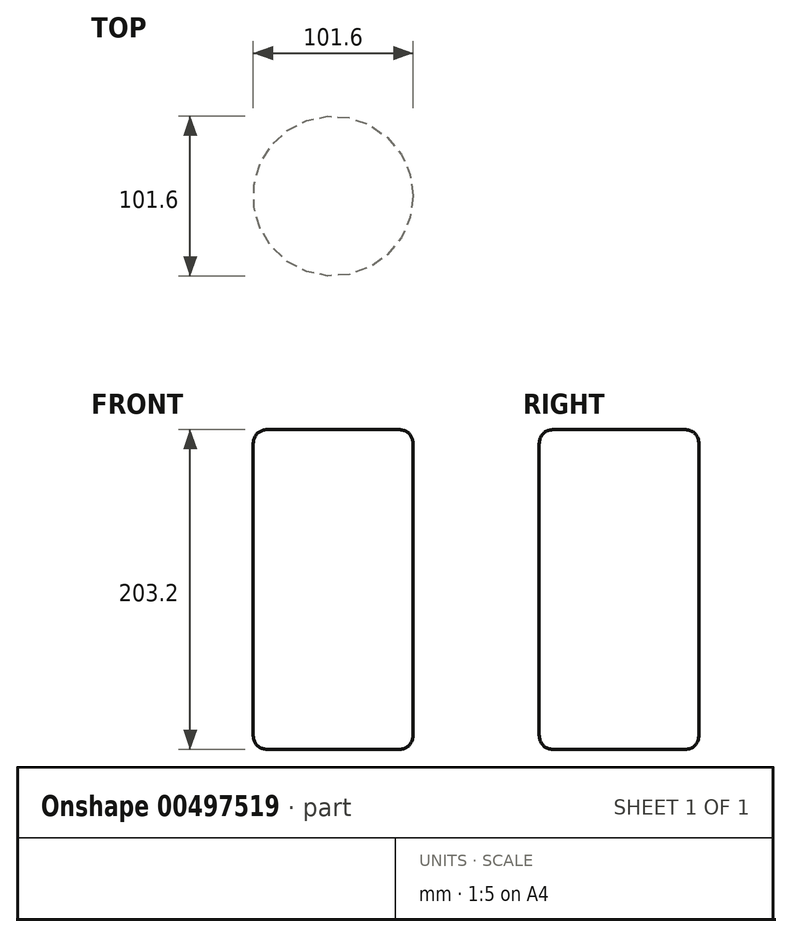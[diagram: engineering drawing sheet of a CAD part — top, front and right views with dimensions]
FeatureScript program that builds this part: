
annotation { "Feature Type Name" : "Feature", "Feature Type Description" : "" }
export const myFeature = defineFeature(function(context is Context, id is Id, definition is map)
    precondition{}
    {
        {
            var Q0;
            Q0=qCreatedBy(makeId("Top.planeOp"),FACE);
            var sketch = newSketch(context, id + "F0", { "sketchPlane" : qUnion([Q0])});
            skCircle(sketch, "E0", {"center": v(0, 0) * mm, "radius": 50.8 * mm});
            skSolve(sketch);
        }
        {
            var Q0;
            Q0=makeQuery(id+"F0.imprint","IMPRINT",FACE,{"disambiguationData":[TD([[makeQuery(id+"F0.imprint","IMPRINT",EDGE,{"derivedFrom":sQuery(id+"F0.wireOp",EDGE,"E0")}),1.0]])]});
            extrude(context, id + "F1", {"entities" : qUnion([Q0]), "depth" : 203.2 * mm});
        }
        {
            var Q0;
            Q0=makeQuery(id+"F1.opExtrude","CAP_FACE",FACE,{"disambiguationData":[OSD([sQuery(id+"F0.wireOp",EDGE,"E0")])],"isStart":true});
            var Q1;
            Q1=makeQuery(id+"F1.opExtrude","CAP_EDGE",EDGE,{"disambiguationData":[OSD([sQuery(id+"F0.wireOp",EDGE,"E0")])],"isStart":false});
            fillet(context, id + "F2", {"entities" : qUnion([Q0, Q1]), "radius" : 10.16 * mm, "tangentPropagation" : true, "rho" : 0.5, "crossSection" : FilletCrossSection.CONIC, "allowEdgeOverflow" : false});
        }
    });
